# Revit family: 24103XXX__
name_source: partatom
category: Plumbing Fixtures
revit_build: Autodesk Revit 2018 (Build: 20170223_1515(x64)
units: mm (PartAtom-declared; Revit-internal decimal feet)

## family parameters
Always vertical = No
Cut with Voids When Loaded = No
OmniClass Number = 23.45.00.00
OmniClass Title = Sanitary, Laundry, and Cleaning Equipment
Part Type = Normal
Room Calculation Point = No
Round Connector Dimension = Use Diameter
Shared = No
Work Plane-Based = No

## types (1)
- 000 Chrome
    Always visible = Yes
    BIMobject category = Showers
    Design country = Germany
    EAN code = 4059625333365
    Edition number = 1
    IFC Classification = Sanitary Terminal
    Installation instructions = https://www.hansgrohe.com
    Manufacturer country = Germany
    Manufacturer name = hansgrohe
    Material 1 = Hansgrohe - Pulsify - Graphite
    Material 2 = Hansgrohe - Pulsify - 000 Chrome
    Material main = Chrome
    Product Guid = c513005c-02a2-44b7-9093-0ead6298d436
    Product SKU = 24103XXX
    Product data url = https://www.bimobject.com
    Product family = Pulsify Blend
    Product group = Hand showers
    Product name = 24103XXX Pulsify Blend Hand shower 105 3jet Activation
    Product url = https://www.hansgrohe.com
    QR code = https://www.bimobject.com
    Technical description = https://www.hansgrohe.com

## geometry (parser evidence)
native form markers: Blend x4, Sweep x3
no freeform markers — native parametric forms only
